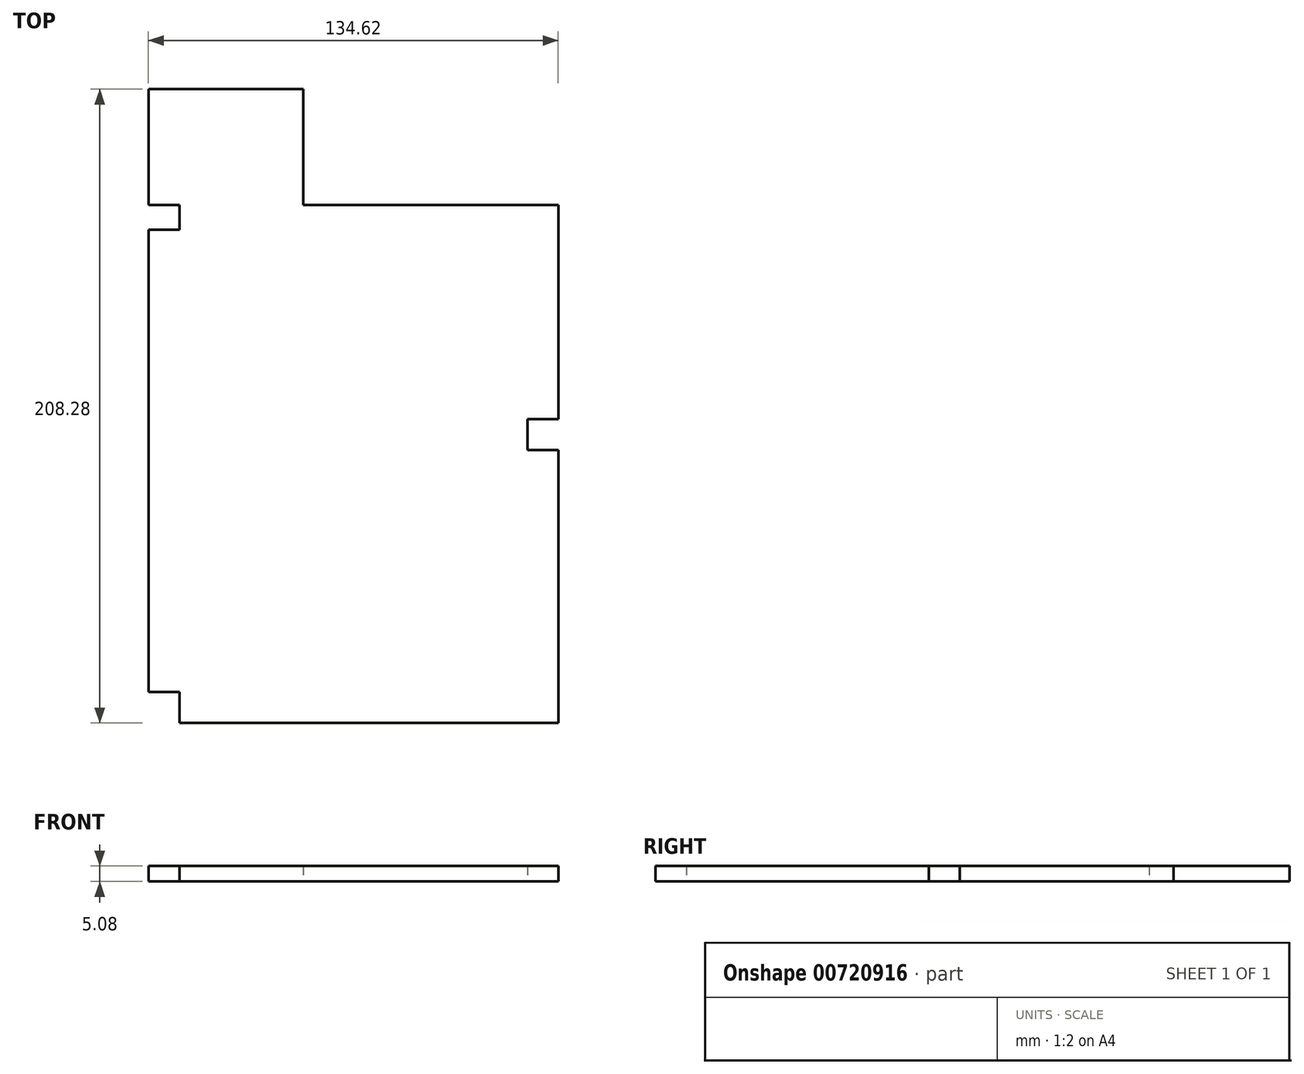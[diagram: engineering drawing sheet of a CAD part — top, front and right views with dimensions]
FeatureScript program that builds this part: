
annotation { "Feature Type Name" : "Feature", "Feature Type Description" : "" }
export const myFeature = defineFeature(function(context is Context, id is Id, definition is map)
    precondition{}
    {
        {
            var Q0;
            Q0=qCreatedBy(makeId("Top.planeOp"),FACE);
            var sketch = newSketch(context, id + "F0", { "sketchPlane" : qUnion([Q0])});
            skLineSegment(sketch, "E0", {"start": v(-54.54, -61.73) * mm, "end": v(-54.54, 146.55) * mm});
            skLineSegment(sketch, "E1", {"start": v(-54.54, 146.55) * mm, "end": v(-3.74, 146.55) * mm});
            skLineSegment(sketch, "E2", {"start": v(-3.74, 146.55) * mm, "end": v(-3.74, 108.45) * mm});
            skLineSegment(sketch, "E3", {"start": v(-3.74, 108.45) * mm, "end": v(80.08, 108.45) * mm});
            skLineSegment(sketch, "E4", {"start": v(80.08, 108.45) * mm, "end": v(80.08, -61.73) * mm});
            skLineSegment(sketch, "E5", {"start": v(80.08, -61.73) * mm, "end": v(-54.54, -61.73) * mm});
            skLineSegment(sketch, "E6", {"start": v(-54.54, 108.45) * mm, "end": v(-44.38, 108.45) * mm});
            skLineSegment(sketch, "E7", {"start": v(-44.38, 108.45) * mm, "end": v(-44.38, 100.36) * mm});
            skLineSegment(sketch, "E8", {"start": v(-44.38, 100.36) * mm, "end": v(-54.54, 100.36) * mm});
            skLineSegment(sketch, "E9", {"start": v(-54.54, 100.36) * mm, "end": v(-54.54, 108.45) * mm});
            skLineSegment(sketch, "E10", {"start": v(-54.54, -61.73) * mm, "end": v(-54.54, -51.57) * mm});
            skLineSegment(sketch, "E11", {"start": v(-54.54, -51.57) * mm, "end": v(-44.38, -51.57) * mm});
            skLineSegment(sketch, "E12", {"start": v(-44.38, -51.57) * mm, "end": v(-44.38, -61.73) * mm});
            skLineSegment(sketch, "E13", {"start": v(80.08, 38.12) * mm, "end": v(69.92, 38.12) * mm});
            skLineSegment(sketch, "E14", {"start": v(69.92, 38.12) * mm, "end": v(69.92, 27.96) * mm});
            skLineSegment(sketch, "E15", {"start": v(69.92, 27.96) * mm, "end": v(80.08, 27.96) * mm});
            skLineSegment(sketch, "E16", {"start": v(80.08, 27.96) * mm, "end": v(80.08, 38.12) * mm});
            skSolve(sketch);
        }
        {
            var Q0;
            {var subQ13=sQuery(id+"F0.wireOp",EDGE,"E1");Q0=makeQuery(id+"F0.imprint","IMPRINT",FACE,{"disambiguationData":[TD([[makeQuery(id+"F0.imprint","IMPRINT",EDGE,{"derivedFrom":subQ13}),-1.0]])]});}
            extrude(context, id + "F1", {"entities" : qUnion([Q0]), "depth" : 5.08 * mm, "offsetDistance" : 25.4 * mm});
        }
    });
